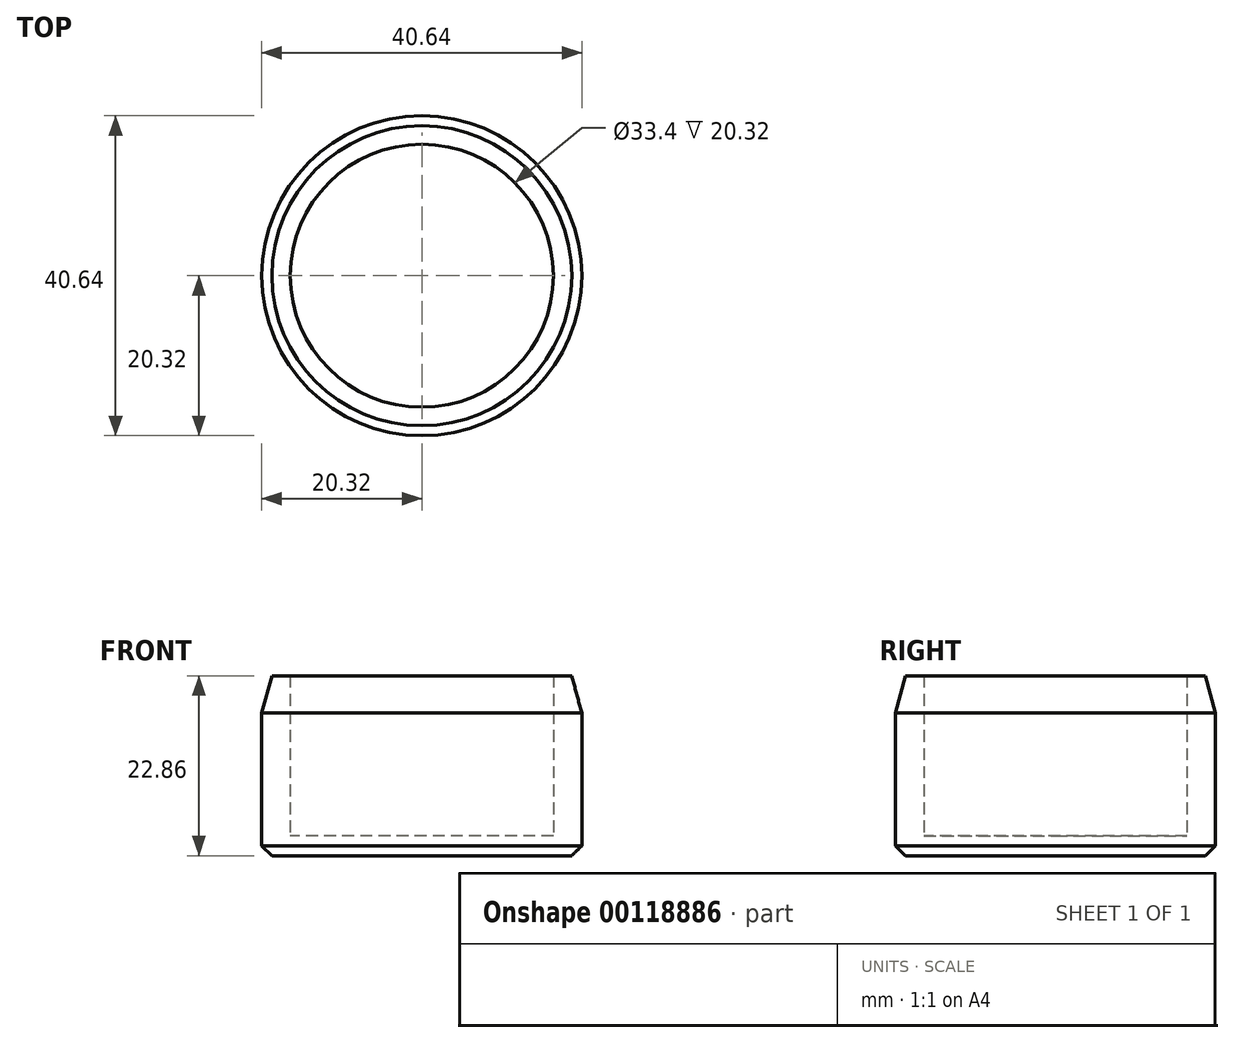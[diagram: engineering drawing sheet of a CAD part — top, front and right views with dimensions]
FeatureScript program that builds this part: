
annotation { "Feature Type Name" : "Feature", "Feature Type Description" : "" }
export const myFeature = defineFeature(function(context is Context, id is Id, definition is map)
    precondition{}
    {
        {
            var Q0;
            Q0=qCreatedBy(makeId("Top.planeOp"),FACE);
            var sketch = newSketch(context, id + "F0", { "sketchPlane" : qUnion([Q0])});
            skCircle(sketch, "E0", {"center": v(0, 0) * mm, "radius": 16.7 * mm});
            skCircle(sketch, "E1", {"center": v(0, 0) * mm, "radius": 20.32 * mm});
            skSolve(sketch);
        }
        {
            var Q0;
            Q0=qSketchRegion(id+"F0",true);
            extrude(context, id + "F1", {"entities" : qUnion([Q0]), "depth" : 22.86 * mm});
        }
        {
            var Q0;
            Q0=makeQuery(id+"F0.imprint","IMPRINT",FACE,{"disambiguationData":[TD([[makeQuery(id+"F0.imprint","IMPRINT",EDGE,{"derivedFrom":sQuery(id+"F0.wireOp",EDGE,"E0")}),1.0]])]});
            var Q1;
            Q1=makeQuery(id+"F0.imprint","IMPRINT",FACE,{"disambiguationData":[TD([[makeQuery(id+"F0.imprint","IMPRINT",EDGE,{"derivedFrom":sQuery(id+"F0.wireOp",EDGE,"E0")}),-1.0]])]});
            extrude(context, id + "F2", {"entities" : qUnion([Q0, Q1]), "operationType" : NewBodyOperationType.ADD, "depth" : 2.54 * mm});
        }
        {
            var Q0;
            Q0=makeQuery(id+"F1.opExtrude","CAP_EDGE",EDGE,{"disambiguationData":[OSD([sQuery(id+"F0.wireOp",EDGE,"E1")])],"isStart":false});
            chamfer(context, id + "F3", {"entities" : qUnion([Q0]), "chamferType" : ChamferType.OFFSET_ANGLE, "width" : 1.27 * mm, "oppositeDirection" : false, "angle" : 75 * degree, "tangentPropagation" : true});
        }
        {
            var Q0;
            Q0=makeQuery(id+"F1.opExtrude","CAP_EDGE",EDGE,{"disambiguationData":[OSD([sQuery(id+"F0.wireOp",EDGE,"E1")])],"isStart":true});
            chamfer(context, id + "F4", {"entities" : qUnion([Q0]), "width" : 1.27 * mm, "tangentPropagation" : true});
        }
    });
